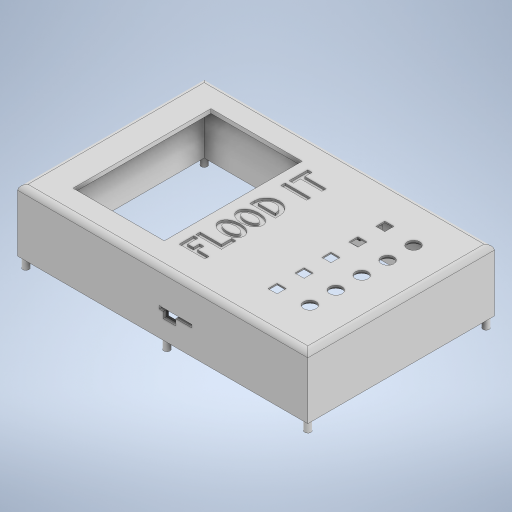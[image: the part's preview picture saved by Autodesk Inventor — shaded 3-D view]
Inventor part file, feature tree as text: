
AUTODESK INVENTOR PART (.ipt)
format: ipt  version: 2023 (Build 270158000, 158)  size: 713,728 bytes
history: native  units: in
note: dims shown in document units (in); Inventor stores cm internally (conversion verified against a paired STEP export)
features: extrude x16, sketch x14, fillet x2
ambient origin geometry x8: Origin, YZ Plane, XZ Plane, XY Plane, X Axis, Y Axis, Z Axis, Center Point
bodies: Solid1 (feature_tree)
feature tree (32):
  extrude  "Extrusion1"  Depth=4.5in
  extrude  "Extrusion2"  Depth=0.2in
  fillet  "Fillet1"  Radius=1.4in
  extrude  "Extrusion3"  Depth=0.125in
  extrude  "Extrusion4"  Depth=2.2in
  extrude  "Extrusion5"  Depth=0.5875in
  sketch  "Sketch6"  dims[d13=0.75in d14=1.4in d15=0.0in]
  extrude  "Extrusion6"  Depth=1.4in TaperAngle=0.0deg
  extrude  "Extrusion9"  Depth=0.1in
  extrude  "Extrusion10"  Depth=0.1in
  extrude  "Extrusion11"  Depth=0.25in
  extrude  "Extrusion12"  Depth=0.15in
  extrude  "Extrusion13"  Depth=0.7in
  extrude  "Extrusion14"  Depth=0.1in
  extrude  "Extrusion15"  Depth=0.615in
  extrude  "Extrusion16"  Depth=0.0625in
  fillet  "Fillet2"  Radius=0.21in
  extrude  "Extrusion18"  Depth=0.0625in
  extrude  "Extrusion19"  Depth=0.0625in
  sketch  "Sketch1"  dims[d0=7.0in d1=4.5in]
  sketch  "Sketch2"  dims[d2=1.5in d3=0.0in d4=0.2in d5=1.4in d6=0.0in]
  sketch  "Sketch3"  dims[d7=0.125in d8=0.25in]
  sketch  "Sketch4"  dims[d9=0.25in d10=2.2in]
  sketch  "Sketch5"  dims[d11=3.325in d12=0.5875in]
  sketch  "Sketch8"  dims[d16=0.1in d17=0.14in]
  sketch  "Sketch9"  dims[d18=0.1in d19=0.275in]
  sketch  "Sketch10"  dims[d20=0.35in d21=0.25in]
  sketch  "Sketch11"  dims[d22=0.15in d23=0.15in]
  sketch  "Sketch12"  dims[d24=0.25in d25=0.7in]
  sketch  "Sketch13"  dims[d26=0.1in d27=0.1in]
  sketch  "Sketch15"  dims[d28=0.25in d29=0.615in]
  sketch  "Sketch16"  dims[d30=0.25in d31=1.1in d32=0.21in d33=0.3075in d34=0.5575in d35=1.65in d36=0.3075in d37=0.21in d38=0.5575in d39=2.1in d40=0.1in d41=0.1in d42=0.3in d43=0.1in d44=0.25in d45=0.615in d46=2.4in d47=0.11in d48=2.51in d49=0.5575in d50=0.1in d51=0.615in d52=0.175in d53=0.175in d54=0.1in d55=0.1in d56=0.25in d57=3.15in d58=0.1in d59=0.515in d60=0.05in d61=0.0in d62=0.1125in d63=0.1125in d64=0.2175in d65=0.2175in d66=0.2175in d67=0.2175in d68=0.2175in d69=0.2175in d70=0.65in d71=0.65in d72=0.65in d73=0.65in d74=0.8413in d76=2.25in d77=0.3in d78=0.3in d79=0.3in d80=0.3in d81=0.3in d82=0.625in d83=0.625in d84=0.625in d85=0.625in d86=1.0in d87=3.1in d88=3.1in d89=3.1in d90=3.1in d91=3.1in d92=1.0in d93=0.0in d97=0.4in d98=0.4in d99=0.4in d100=0.4in d101=0.4in d102=0.05in d103=0.0in d124=0.0688in d125=0.0in d126=0.25in d127=0.275in d128=0.25in d129=0.25in d130=0.25in d131=2.1in d132=0.2in d134=0.05in d135=0.0in d142=0.0375in d143=0.0in d144=2.0in d145=0.785in d146=0.0725in d147=0.3in d148=0.15in d149=0.1in d150=0.7in d151=0.2in d152=0.0in d153=0.075in d154=0.125in d155=0.0in d156=0.285in d157=2.5in d158=0.49in d159=0.25in d160=0.0in d161=0.49in d162=0.081in d163=0.0in d164=0.45in d177=0.075in d178=0.0in d179=0.125in d187=2.8in d189=0.04in d190=0.04in d191=0.04in d192=0.04in d193=0.04in d194=0.485in d195=0.0938in d197=3.325in d198=0.254in d199=0.1735in d202=0.075in d203=0.125in d204=0.075in d205=0.125in d206=0.1875in d207=0.1875in d208=0.1875in d209=0.65in d210=0.65in d211=0.65in d212=0.125in d213=0.075in d214=0.025in d215=2.0in d216=0.5in d217=0.0in d218=0.0in d219=0.285in d220=0.1425in d221=0.245in d222=0.285in d224=0.8413in d225=0.15in d226=0.15in d227=0.15in d228=0.15in d229=0.15in d230=0.15in d231=0.1in d232=0.1in d233=0.1in d234=0.1in d235=0.1in d236=0.1in d237=0.1in d238=0.1in d239=0.1in d240=0.1in d241=3.5in d242=3.5in d243=0.245in d244=0.0in d245=0.0625in]
